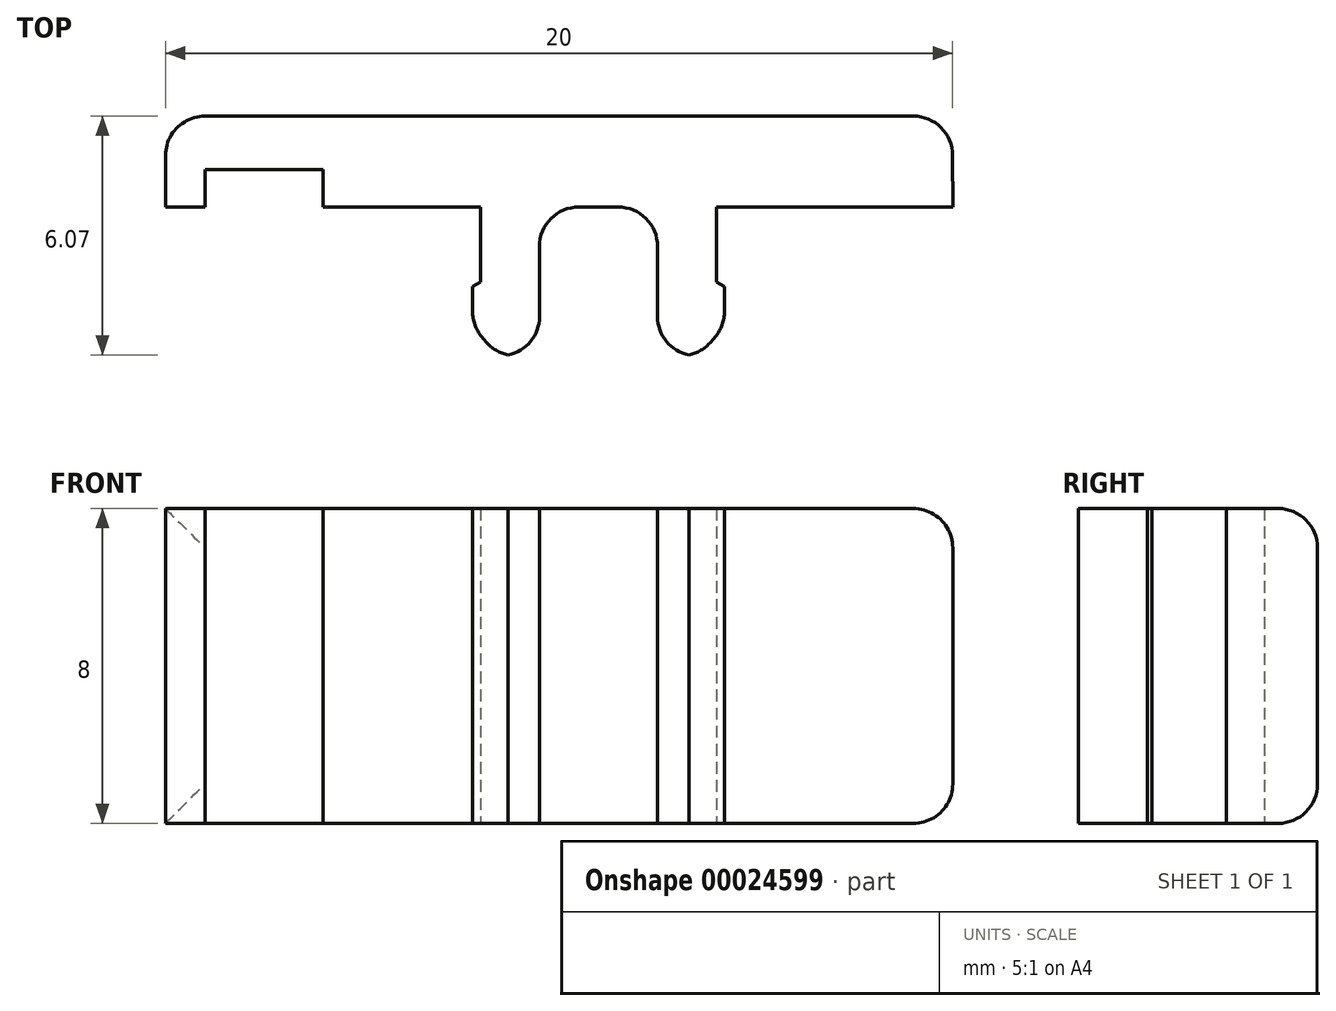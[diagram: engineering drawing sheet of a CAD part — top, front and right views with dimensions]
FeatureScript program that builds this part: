
annotation { "Feature Type Name" : "Feature", "Feature Type Description" : "" }
export const myFeature = defineFeature(function(context is Context, id is Id, definition is map)
    precondition{}
    {
        {
            var Q0;
            Q0=qCreatedBy(makeId("Top.planeOp"),FACE);
            var sketch = newSketch(context, id + "F0", { "sketchPlane" : qUnion([Q0])});
            skLineSegment(sketch, "E0", {"start": v(16.12, 0) * mm, "end": v(10.12, 0) * mm});
            skLineSegment(sketch, "E1", {"start": v(10.12, 0) * mm, "end": v(10.12, -1.9) * mm});
            skLineSegment(sketch, "E2", {"start": v(10.12, -1.9) * mm, "end": v(10.32, -2.02) * mm});
            skLineSegment(sketch, "E3", {"start": v(10.32, -2.02) * mm, "end": v(10.32, -3.02) * mm});
            skLineSegment(sketch, "E4", {"start": v(10.32, -3.02) * mm, "end": v(9.68, -3.78) * mm});
            skLineSegment(sketch, "E5", {"start": v(9.68, -3.78) * mm, "end": v(8.62, -3.78) * mm});
            skLineSegment(sketch, "E6", {"start": v(4.12, 0) * mm, "end": v(0.12, 0) * mm});
            skLineSegment(sketch, "E7", {"start": v(0.12, 0) * mm, "end": v(0.12, 0.95) * mm});
            skLineSegment(sketch, "E8", {"start": v(0.12, 0.95) * mm, "end": v(-2.88, 0.95) * mm});
            skLineSegment(sketch, "E9", {"start": v(-2.88, 0.95) * mm, "end": v(-2.88, 0) * mm});
            skLineSegment(sketch, "E10", {"start": v(-2.88, 0) * mm, "end": v(-3.88, 0) * mm});
            skLineSegment(sketch, "E11", {"start": v(-3.88, 0) * mm, "end": v(-3.88, 2.3) * mm});
            skLineSegment(sketch, "E12", {"start": v(-3.88, 2.3) * mm, "end": v(16.12, 2.3) * mm});
            skLineSegment(sketch, "E13", {"start": v(16.12, 2.3) * mm, "end": v(16.12, 0) * mm});
            skLineSegment(sketch, "E14", {"start": v(7.12, 0) * mm, "end": v(8.62, 0) * mm});
            skLineSegment(sketch, "E15", {"start": v(8.62, 0) * mm, "end": v(8.62, -3.78) * mm});
            skLineSegment(sketch, "E16", {"start": v(7.12, 4.05) * mm, "end": v(7.12, -5.04) * mm, "construction": true});
            skLineSegment(sketch, "E17.MirrorCS", {"start": v(7.12, 0) * mm, "end": v(5.62, 0) * mm});
            skLineSegment(sketch, "E18.MirrorCS", {"start": v(5.62, 0) * mm, "end": v(5.62, -3.78) * mm});
            skLineSegment(sketch, "E19.MirrorCS", {"start": v(4.57, -3.78) * mm, "end": v(5.62, -3.78) * mm});
            skLineSegment(sketch, "E20.MirrorCS", {"start": v(3.92, -3.02) * mm, "end": v(4.57, -3.78) * mm});
            skLineSegment(sketch, "E21.MirrorCS", {"start": v(3.92, -2.02) * mm, "end": v(3.92, -3.02) * mm});
            skLineSegment(sketch, "E22.MirrorCS", {"start": v(4.12, -1.9) * mm, "end": v(3.92, -2.02) * mm});
            skLineSegment(sketch, "E23.MirrorCS", {"start": v(4.12, 0) * mm, "end": v(4.12, -1.9) * mm});
            skSolve(sketch);
        }
        {
            var Q0;
            Q0 = qSketchRegion(id + "F0", true);
            extrude(context, id + "F1", {"entities" : qUnion([Q0]), "depth" : 8 * mm});
        }
        {
            var Q0;
            Q0=makeQuery(id+"F1.opExtrude","SWEPT_EDGE",EDGE,{"disambiguationData":[OSD([sQuery(id+"F0.wireOp",EDGE,"E20.MirrorCS"),sQuery(id+"F0.wireOp",EDGE,"E21.MirrorCS")])]});
            var Q1;
            Q1=makeQuery(id+"F1.opExtrude","SWEPT_EDGE",EDGE,{"disambiguationData":[OSD([sQuery(id+"F0.wireOp",EDGE,"E3"),sQuery(id+"F0.wireOp",EDGE,"E4")])]});
            var Q2;
            Q2=makeQuery(id+"F1.opExtrude","SWEPT_EDGE",EDGE,{"disambiguationData":[OSD([sQuery(id+"F0.wireOp",EDGE,"E19.MirrorCS"),sQuery(id+"F0.wireOp",EDGE,"E20.MirrorCS")])]});
            var Q3;
            Q3=makeQuery(id+"F1.opExtrude","SWEPT_EDGE",EDGE,{"disambiguationData":[OSD([sQuery(id+"F0.wireOp",EDGE,"E4"),sQuery(id+"F0.wireOp",EDGE,"E5")])]});
            var Q4;
            Q4=makeQuery(id+"F1.opExtrude","SWEPT_EDGE",EDGE,{"disambiguationData":[OSD([sQuery(id+"F0.wireOp",EDGE,"E5"),sQuery(id+"F0.wireOp",EDGE,"E15")])]});
            var Q5;
            Q5=makeQuery(id+"F1.opExtrude","SWEPT_EDGE",EDGE,{"disambiguationData":[OSD([sQuery(id+"F0.wireOp",EDGE,"E18.MirrorCS"),sQuery(id+"F0.wireOp",EDGE,"E19.MirrorCS")])]});
            var Q6;
            Q6=makeQuery(id+"F1.opExtrude","SWEPT_EDGE",EDGE,{"disambiguationData":[OSD([sQuery(id+"F0.wireOp",EDGE,"E14"),sQuery(id+"F0.wireOp",EDGE,"E15")])]});
            var Q7;
            Q7=makeQuery(id+"F1.opExtrude","SWEPT_EDGE",EDGE,{"disambiguationData":[OSD([sQuery(id+"F0.wireOp",EDGE,"E17.MirrorCS"),sQuery(id+"F0.wireOp",EDGE,"E18.MirrorCS")])]});
            var Q8;
            Q8=makeQuery(id+"F1.opExtrude","SWEPT_FACE",FACE,{"disambiguationData":[OSD([sQuery(id+"F0.wireOp",EDGE,"E12")])]});
            var Q9;
            Q9=makeQuery(id+"F1.opExtrude","CAP_EDGE",EDGE,{"disambiguationData":[OSD([sQuery(id+"F0.wireOp",EDGE,"E13")])],"isStart":false});
            var Q10;
            Q10=makeQuery(id+"F1.opExtrude","CAP_EDGE",EDGE,{"disambiguationData":[OSD([sQuery(id+"F0.wireOp",EDGE,"E13")])],"isStart":true});
            fillet(context, id + "F2", {"entities" : qUnion([Q0, Q1, Q2, Q3, Q4, Q5, Q6, Q7, Q8, Q9, Q10]), "radius" : 1 * mm, "allowEdgeOverflow" : false});
        }
    });
